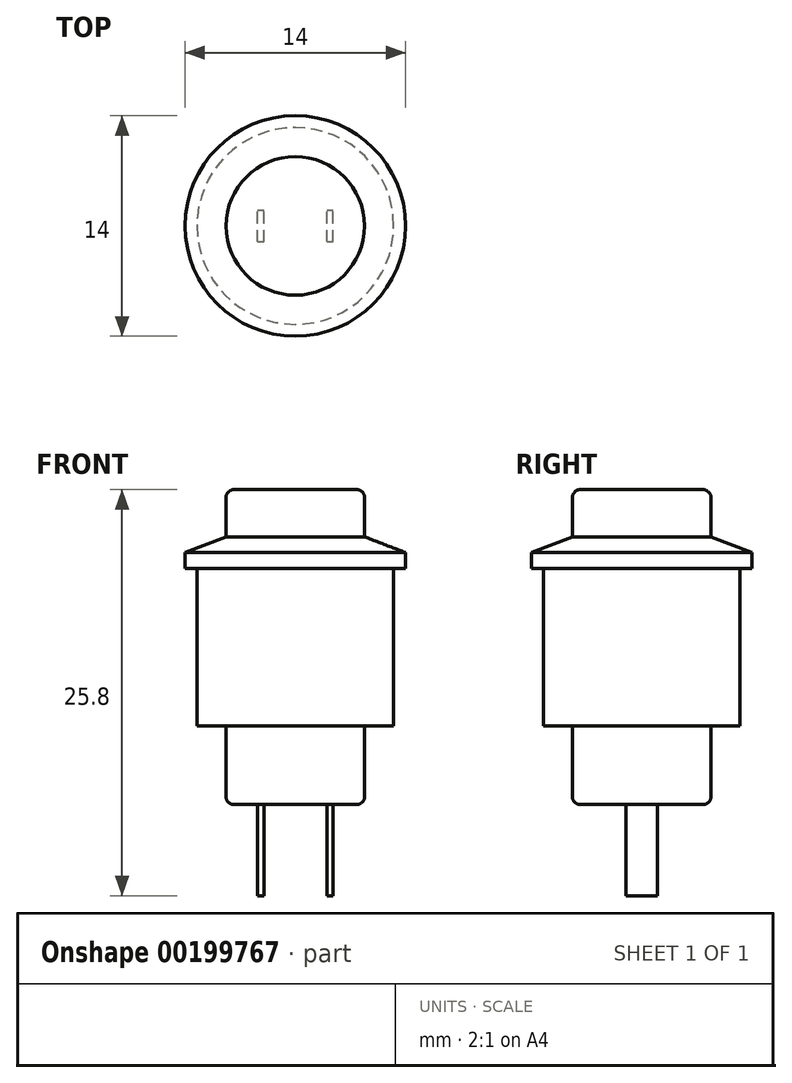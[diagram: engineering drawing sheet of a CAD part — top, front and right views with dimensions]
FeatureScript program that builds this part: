
annotation { "Feature Type Name" : "Feature", "Feature Type Description" : "" }
export const myFeature = defineFeature(function(context is Context, id is Id, definition is map)
    precondition{}
    {
        {
            var Q0;
            Q0=qCreatedBy(makeId("Top.planeOp"),FACE);
            var sketch = newSketch(context, id + "F0", { "sketchPlane" : qUnion([Q0])});
            skCircle(sketch, "E0", {"center": v(0, 0) * mm, "radius": 4.4 * mm});
            skSolve(sketch);
        }
        {
            var Q0;
            Q0=makeQuery(id+"F0.imprint","IMPRINT",FACE,{"disambiguationData":[TD([[makeQuery(id+"F0.imprint","IMPRINT",EDGE,{"derivedFrom":sQuery(id+"F0.wireOp",EDGE,"E0")}),1.0]])]});
            extrude(context, id + "F1", {"entities" : qUnion([Q0]), "depth" : 20 * mm});
        }
        {
            var Q0;
            Q0=makeQuery(id+"F1.opExtrude","CAP_EDGE",EDGE,{"disambiguationData":[OSD([sQuery(id+"F0.wireOp",EDGE,"E0")])],"isStart":false});
            var Q1;
            Q1=makeQuery(id+"F1.opExtrude","CAP_EDGE",EDGE,{"disambiguationData":[OSD([sQuery(id+"F0.wireOp",EDGE,"E0")])],"isStart":true});
            fillet(context, id + "F2", {"entities" : qUnion([Q0, Q1]), "radius" : 0.5 * mm, "tangentPropagation" : true, "allowEdgeOverflow" : false});
        }
        {
            var Q0;
            Q0=makeQuery(id+"F1.opExtrude","CAP_FACE",FACE,{"disambiguationData":[OSD([sQuery(id+"F0.wireOp",EDGE,"E0")])],"isStart":false});
            cPlane(context, id + "F3", {"entities" : qUnion([Q0]), "cplaneType" : CPlaneType.OFFSET, "offset" : 3 * mm, "oppositeDirection" : true, "width" : 150 * mm, "height" : 150 * mm});
        }
        {
            var Q0;
            Q0=qCreatedBy(id+"F3.planeOp",FACE);
            var sketch = newSketch(context, id + "F4", { "sketchPlane" : qUnion([Q0])});
            skCircle(sketch, "E1", {"center": v(0, 0) * mm, "radius": 7 * mm});
            skSolve(sketch);
        }
        {
            var Q0;
            Q0=makeQuery(id+"F4.imprint","IMPRINT",FACE,{"disambiguationData":[TD([[makeQuery(id+"F4.imprint","IMPRINT",EDGE,{"derivedFrom":sQuery(id+"F4.wireOp",EDGE,"E1")}),1.0]])]});
            extrude(context, id + "F5", {"entities" : qUnion([Q0]), "operationType" : NewBodyOperationType.ADD, "oppositeDirection" : true, "depth" : 12 * mm});
        }
        {
            var Q0;
            Q0=makeQuery(id+"F1.opExtrude","CAP_FACE",FACE,{"disambiguationData":[OSD([sQuery(id+"F0.wireOp",EDGE,"E0")])],"isStart":true});
            var sketch = newSketch(context, id + "F6", { "sketchPlane" : qUnion([Q0])});
            skLineSegment(sketch, "E2.bottom", {"start": v(-2.4, 1) * mm, "end": v(-2, 1) * mm});
            skLineSegment(sketch, "E2.top", {"start": v(-2.4, -1) * mm, "end": v(-2, -1) * mm});
            skLineSegment(sketch, "E2.left", {"start": v(-2.4, 1) * mm, "end": v(-2.4, -1) * mm});
            skLineSegment(sketch, "E2.right", {"start": v(-2, 1) * mm, "end": v(-2, -1) * mm});
            skLineSegment(sketch, "E3.bottom", {"start": v(2, 1) * mm, "end": v(2.4, 1) * mm});
            skLineSegment(sketch, "E3.top", {"start": v(2, -1) * mm, "end": v(2.4, -1) * mm});
            skLineSegment(sketch, "E3.left", {"start": v(2, 1) * mm, "end": v(2, -1) * mm});
            skLineSegment(sketch, "E3.right", {"start": v(2.4, 1) * mm, "end": v(2.4, -1) * mm});
            skSolve(sketch);
        }
        {
            var Q0;
            Q0=makeQuery(id+"F6.imprint","IMPRINT",FACE,{"disambiguationData":[TD([[makeQuery(id+"F6.imprint","IMPRINT",EDGE,{"derivedFrom":sQuery(id+"F6.wireOp",EDGE,"E2.bottom")}),-1.0]])]});
            var Q1;
            Q1=makeQuery(id+"F6.imprint","IMPRINT",FACE,{"disambiguationData":[TD([[makeQuery(id+"F6.imprint","IMPRINT",EDGE,{"derivedFrom":sQuery(id+"F6.wireOp",EDGE,"E3.bottom")}),-1.0]])]});
            extrude(context, id + "F7", {"entities" : qUnion([Q0, Q1]), "operationType" : NewBodyOperationType.ADD, "depth" : 5.8 * mm});
        }
        {
            var Q0;
            Q0=makeQuery(id+"F5.opExtrude","CAP_EDGE",EDGE,{"disambiguationData":[OSD([sQuery(id+"F4.wireOp",EDGE,"E1")])],"isStart":true});
            chamfer(context, id + "F8", {"entities" : qUnion([Q0]), "chamferType" : ChamferType.TWO_OFFSETS, "width1" : 2.6 * mm, "oppositeDirection" : false, "width2" : 1 * mm, "tangentPropagation" : true});
        }
        {
            var Q0;
            Q0=makeQuery(id+"F5.opExtrude","CAP_FACE",FACE,{"disambiguationData":[OSD([sQuery(id+"F4.wireOp",EDGE,"E1")])],"isStart":false});
            var sketch = newSketch(context, id + "F9", { "sketchPlane" : qUnion([Q0])});
            skCircle(sketch, "E4", {"center": v(0, 0) * mm, "radius": 6.25 * mm});
            skSolve(sketch);
        }
        {
            var Q0;
            Q0=makeQuery(id+"F9.imprint","IMPRINT",FACE,{"disambiguationData":[TD([[makeQuery(id+"F9.imprint","IMPRINT",EDGE,{"derivedFrom":sQuery(id+"F9.wireOp",EDGE,"E4")}),-1.0]])]});
            extrude(context, id + "F10", {"entities" : qUnion([Q0]), "operationType" : NewBodyOperationType.REMOVE, "oppositeDirection" : true, "depth" : 10 * mm});
        }
    });
